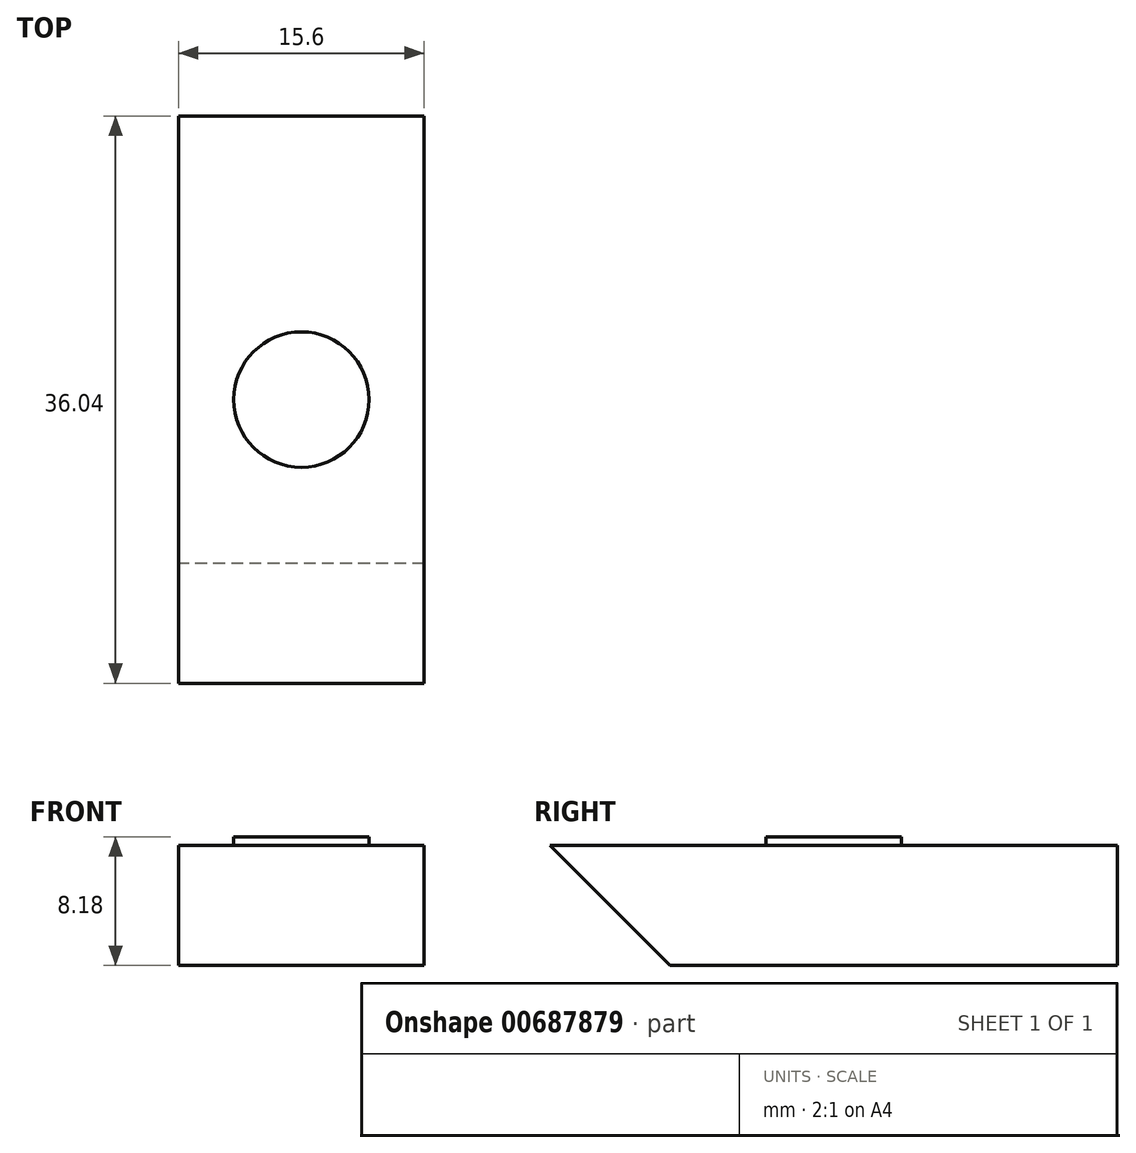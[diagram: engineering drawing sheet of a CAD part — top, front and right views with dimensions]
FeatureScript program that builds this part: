
annotation { "Feature Type Name" : "Feature", "Feature Type Description" : "" }
export const myFeature = defineFeature(function(context is Context, id is Id, definition is map)
    precondition{}
    {
        {
            var Q0;
            Q0=qCreatedBy(makeId("Top.planeOp"),FACE);
            var sketch = newSketch(context, id + "F0", { "sketchPlane" : qUnion([Q0])});
            skLineSegment(sketch, "E0.bottom", {"start": v(7.8, -18.02) * mm, "end": v(-7.8, -18.02) * mm});
            skLineSegment(sketch, "E0.top", {"start": v(7.8, 18.02) * mm, "end": v(-7.8, 18.02) * mm});
            skLineSegment(sketch, "E0.left", {"start": v(7.8, -18.02) * mm, "end": v(7.8, 18.02) * mm});
            skLineSegment(sketch, "E0.right", {"start": v(-7.8, -18.02) * mm, "end": v(-7.8, 18.02) * mm});
            skPoint(sketch, "E0.middle", {"position": v(0, 0) * mm});
            skSolve(sketch);
        }
        {
            var Q0;
            Q0 = qSketchRegion(id + "F0", true);
            extrude(context, id + "F1", {"entities" : qUnion([Q0]), "depth" : 7.62 * mm, "offsetDistance" : 25.4 * mm});
        }
        {
            var Q0;
            Q0=makeQuery(id+"F1.opExtrude","CAP_EDGE",EDGE,{"disambiguationData":[OSD([sQuery(id+"F0.wireOp",EDGE,"E0.bottom")])],"isStart":true});
            chamfer(context, id + "F2", {"entities" : qUnion([Q0]), "width" : 7.62 * mm, "tangentPropagation" : true});
        }
        {
            var Q0;
            Q0=makeQuery(id+"F1.opExtrude","CAP_FACE",FACE,{"disambiguationData":[OSD([sQuery(id+"F0.wireOp",EDGE,"E0.bottom"),sQuery(id+"F0.wireOp",EDGE,"E0.top"),sQuery(id+"F0.wireOp",EDGE,"E0.left"),sQuery(id+"F0.wireOp",EDGE,"E0.right")])],"isStart":false});
            var sketch = newSketch(context, id + "F3", { "sketchPlane" : qUnion([Q0])});
            skCircle(sketch, "E1", {"center": v(0, 0) * mm, "radius": 4.3 * mm});
            skSolve(sketch);
        }
        {
            var Q0;
            Q0 = qSketchRegion(id + "F3", true);
            extrude(context, id + "F4", {"entities" : qUnion([Q0]), "operationType" : NewBodyOperationType.ADD, "depth" : 0.56 * mm, "offsetDistance" : 25.4 * mm});
        }
    });
